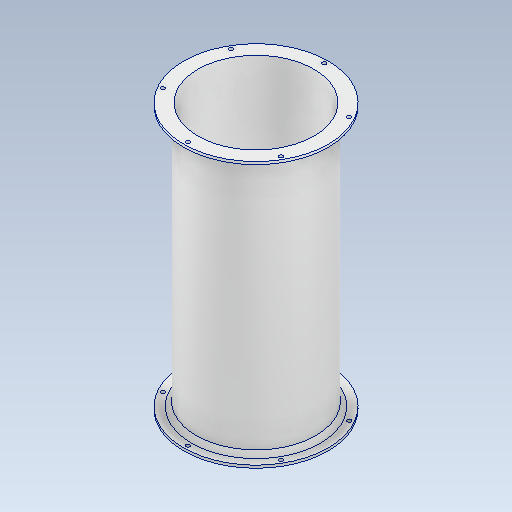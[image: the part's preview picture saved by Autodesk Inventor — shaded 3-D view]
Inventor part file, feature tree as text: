
AUTODESK INVENTOR PART (.ipt)
format: ipt  version: 2021 (Build 250183000, 183)  size: 175,104 bytes
history: native  units: mm
features: revolve x1, hole x1, mirror x1, sketch x1, projected_geometry x1
ambient origin geometry x8: Origin, YZ Plane, XZ Plane, XY Plane, X Axis, Y Axis, Z Axis, Center Point
bodies: Solid1 (feature_tree)
feature tree (5):
  revolve  "Revolution1"  Angle=90.0deg
  hole  "Hole1"  [1 undecoded]
  mirror  "Mirror1"
  sketch  "Sketch2"  dims[d0=300.0mm d3=90.0deg d5=81.5mm d6=2.0mm d7=9.0mm d8=5.0mm d9=45.0deg d10=16.0mm d11=3.0mm d12=3.0mm d13=9.0mm d14=45.0deg d15=5.0mm d16=4.5mm d17=8.0mm d18=60.0mm d20=360.0deg d22=4.5mm d23=10.0mm d24=9.4mm d25=2.0mm d26=90.0deg d27=13.0mm d28=20.594885mm d29=4.5mm]
  projected_geometry  "Projected Loop1"
note: 1 required parameter value undecoded (feature->parameter linkage not recoverable at this tier; creation-order binding heuristic only, values carry confidence <= 0.55)
